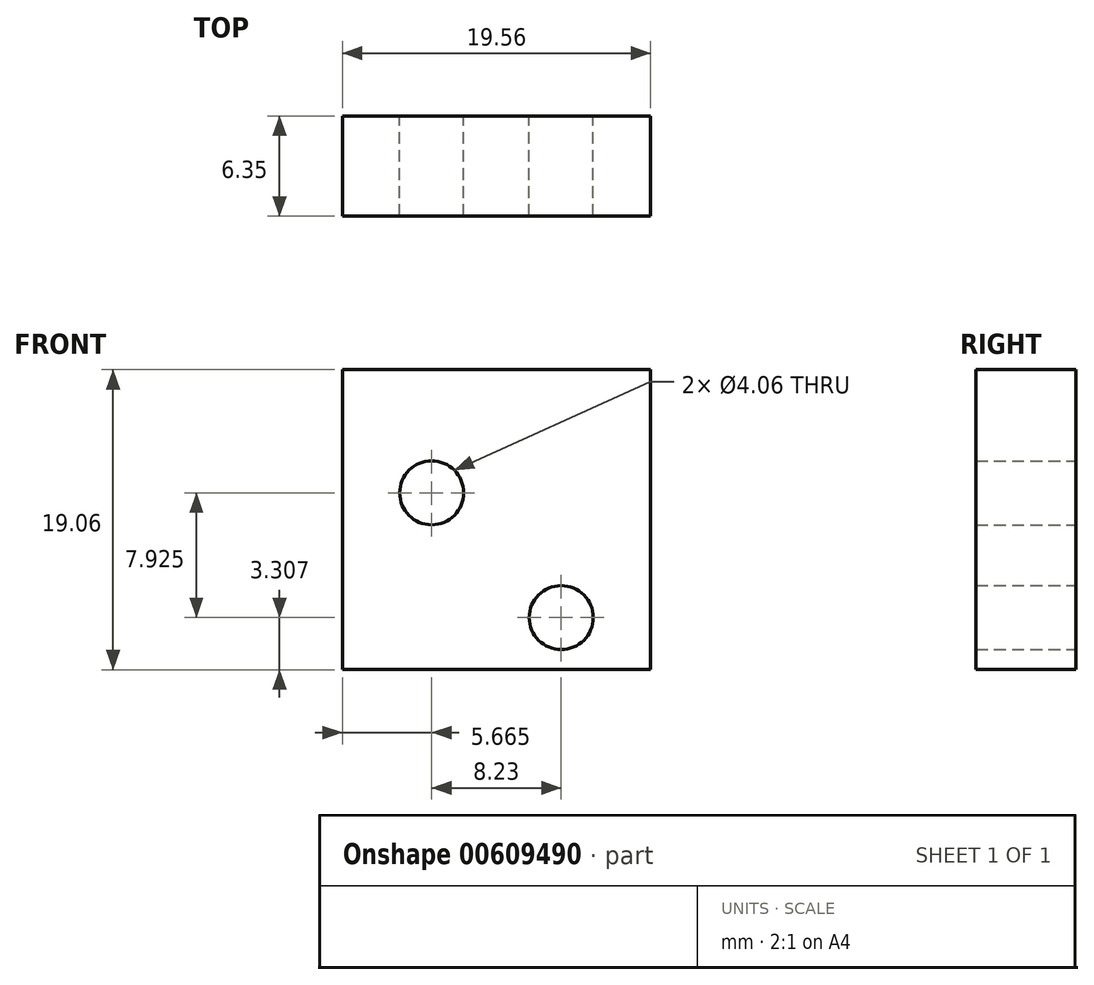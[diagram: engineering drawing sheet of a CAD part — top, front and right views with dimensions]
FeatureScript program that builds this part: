
annotation { "Feature Type Name" : "Feature", "Feature Type Description" : "" }
export const myFeature = defineFeature(function(context is Context, id is Id, definition is map)
    precondition{}
    {
        {
            var Q0;
            Q0=qCreatedBy(makeId("Front.planeOp"),FACE);
            var sketch = newSketch(context, id + "F0", { "sketchPlane" : qUnion([Q0])});
            skLineSegment(sketch, "E0.bottom", {"start": v(9.78, -9.52) * mm, "end": v(-9.78, -9.53) * mm});
            skLineSegment(sketch, "E0.top", {"start": v(9.78, 9.53) * mm, "end": v(-9.78, 9.52) * mm});
            skLineSegment(sketch, "E0.left", {"start": v(9.78, -9.52) * mm, "end": v(9.78, 9.53) * mm});
            skLineSegment(sketch, "E0.right", {"start": v(-9.78, -9.53) * mm, "end": v(-9.78, 9.52) * mm});
            skPoint(sketch, "E0.middle", {"position": v(0, 0) * mm});
            skCircle(sketch, "E1", {"center": v(-4.11, 1.7) * mm, "radius": 2.03 * mm});
            skCircle(sketch, "E2", {"center": v(4.11, -6.22) * mm, "radius": 2.03 * mm});
            skSolve(sketch);
        }
        {
            var Q0;
            Q0=makeQuery(id+"F0.imprint","IMPRINT",FACE,{"disambiguationData":[TD([[makeQuery(id+"F0.imprint","IMPRINT",EDGE,{"derivedFrom":sQuery(id+"F0.wireOp",EDGE,"E0.bottom")}),-1.0]])]});
            extrude(context, id + "F1", {"entities" : qUnion([Q0]), "depth" : 6.35 * mm, "offsetDistance" : 25.4 * mm});
        }
    });
